# Revit family: RN 91062 Optifitt-Serra-Rohrnippel
name_source: partatom
category: Rohrformteile
units: mm (PartAtom-declared; Revit-internal decimal feet)

## family parameters
Arbeitsebenenbasiert = Nein
Beim Laden mit Abzugskörper schneiden = Nein
Bemaßung runder Anschluss = Durchmesser verwenden
Gemeinsam genutzt = Nein
Immer vertikal = Ja
Teiletyp = Nicht definiert

## types (4) — shared parameters
1.010.00.2 Blattnummer der Richtlinie = 29
1.010.00.3 Ausgabedatum (Monat) der Richtlinie = 201308
1.010.00.4 Herstellername = R. Nussbaum AG
1.010.00.5 Revisionsdatum der Datei = 20190521
1.010.00.6 Webadresse des Herstellers = http://www.nussbaum.ch
1.100.00.4 Produktbezeichnung = Versorgung
1.110.00.2 Index = 3
1.110.00.4 Produktbezeichnung = Optifitt-Serra
1.960/3L.00.8 Link (URL) = https://www.nussbaum.ch
29.700.00.4 Produktname = Optifitt-Serra-Rohrnippel
29.700.00.5 Produktkennung = 2
29.700.00.6 Querschnittsform = 1
29.700.00.7 Nennweitensystem = DN
29.700.00.8 Nenndrucksystem = PN
29.710.02.4 Nenndruck = 16
29.710.02.5 max. zul. Überdruck [hPa] = 1600
29.710.02.7 max. zul. Dauer-Betriebsdruck [hPa] = 1600
29.710.02.9 max. zul. Dauer-Betriebstemperatur [°C] = 90
CONNECTOR0_DIAMETER_dX_0r = 15 mm
CONNECTOR0_dX_01 = 13 mm
CONNECTOR0_ref_dX = 13 mm
CONNECTOR1_DIAMETER_dX_0r = 15 mm
Connector Visibility = Nein
EnclosingSpace Visibility = Nein
Hersteller = R. Nussbaum AG
Typenkommentare = Optifitt-Serra-Rohrnippel  DN=15
URL = https://www.nussbaum.ch

## per-type parameters (varying)
| type | 1.800.00.3 TGA-Nummer | 1.800.00.4 Kommentarfeld | 1.810.00.3 Hersteller-Bestellnummer | 1.810.00.4 DATANORM-Nummer | 1.810.00.5 StLB-Nummer | 1.810.00.6 GTIN-Nummer | 29.710.02.10 Formstück-Gewicht [kg] | 29.710.02.3 Benennung | CONNECTOR1_dX_00 | CONNECTOR1_dX_01 | CONNECTOR1_ref_dX | CONNECTOR1_ref_dX2 | Modell | R. Nussbaum AG 91062.77 de Visibility | R. Nussbaum AG 91062.78 de Visibility | R. Nussbaum AG 91062.79 de Visibility | R. Nussbaum AG 91062.80 de Visibility |
| DN=2 | 01900300000000000000000000000000000000000000000019000000000000000076 | 91062.80, Optifitt-Serra-Rohrnippel, DN=15, L=100, R=½ | 91062.8 | 91062.8 |  | 7612945036605 | 0.165 | Optifitt-Serra-Rohrnippel, DN=15, L=100, R=½ | 85 mm | 98 mm | 85 mm | 98 mm | 91062.8 | Nein | Nein | Nein | Ja |
| DN=15 | 01900300000000000000000000000000000000000000000019000000000000000067 | 91062.79, Optifitt-Serra-Rohrnippel, DN=15, L=80, R=½ | 91062.79 | 91062.79 |  | 7612945036599 | 0.128 | Optifitt-Serra-Rohrnippel, DN=15, L=80, R=½ | 65 mm | 78 mm | 65 mm | 78 mm | 91062.79 | Nein | Nein | Ja | Nein |
| DN=3 | 01900300000000000000000000000000000000000000000019000000000000000066 | 91062.78, Optifitt-Serra-Rohrnippel, DN=15, L=60, R=½ | 91062.78 | 91062.78 |  | 7612945036582 | 0.09 | Optifitt-Serra-Rohrnippel, DN=15, L=60, R=½ | 45 mm | 58 mm  [stored 0.190289 ft] | 45 mm | 58 mm  [stored 0.190289 ft] | 91062.78 | Nein | Ja | Nein | Nein |
| DN=1 | 01900300000000000000000000000000000000000000000019000000000000000065 | 91062.77, Optifitt-Serra-Rohrnippel, DN=15, L=40, R=½ | 91062.77 | 91062.77 | 214.232 | 7612945036575 | 0.054 | Optifitt-Serra-Rohrnippel, DN=15, L=40, R=½ | 25 mm  [stored 0.082021 ft] | 38 mm | 25 mm  [stored 0.082021 ft] | 38 mm | 91062.77 | Ja | Nein | Nein | Nein |

note: [stored X ft] marks values corroborated as IEEE doubles in the binary element streams (Revit-internal decimal feet)

## geometry (parser evidence)
native form markers: Sweep x2
no freeform markers — native parametric forms only
